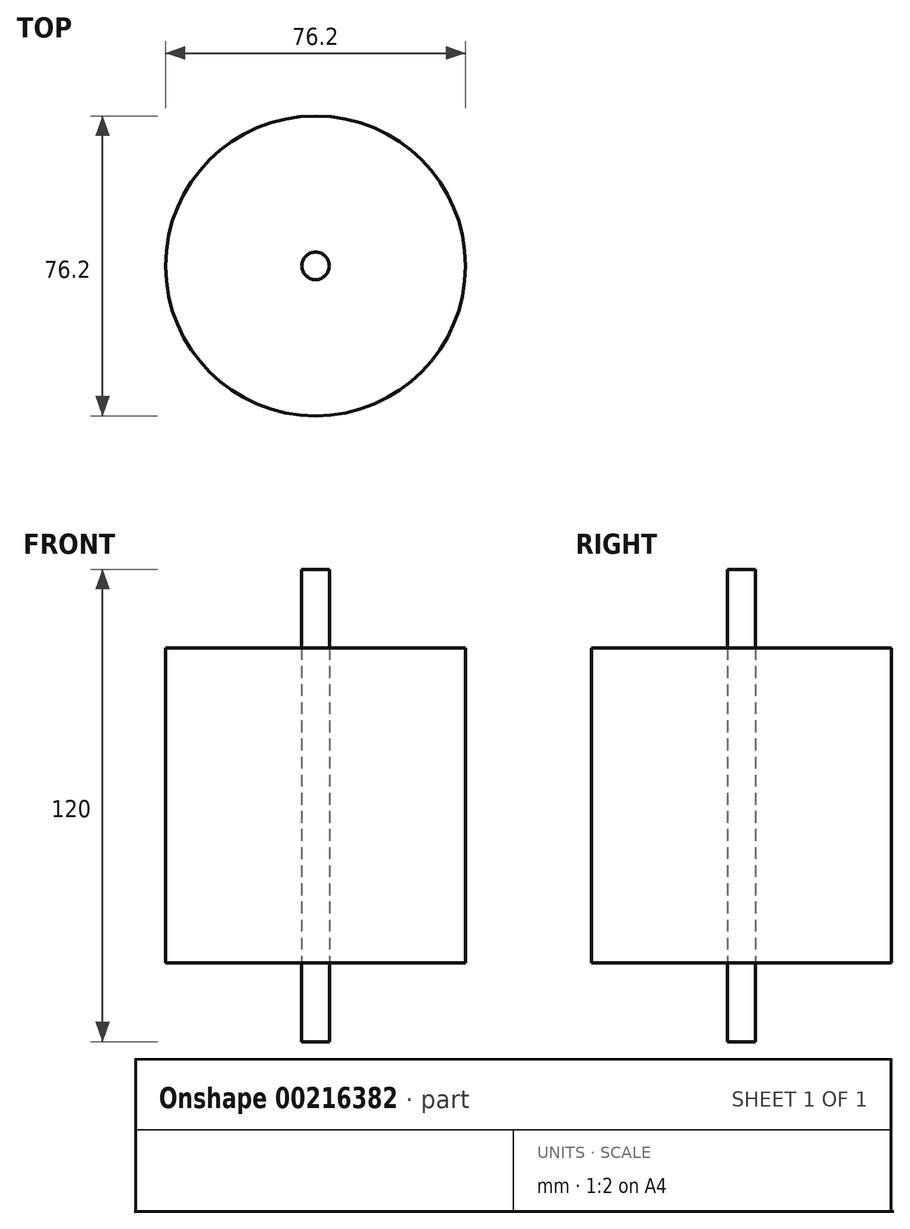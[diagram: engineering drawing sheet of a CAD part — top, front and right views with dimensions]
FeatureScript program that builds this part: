
annotation { "Feature Type Name" : "Feature", "Feature Type Description" : "" }
export const myFeature = defineFeature(function(context is Context, id is Id, definition is map)
    precondition{}
    {
        {
            var Q0;
            Q0=qCreatedBy(makeId("Top.planeOp"),FACE);
            var sketch = newSketch(context, id + "F0", { "sketchPlane" : qUnion([Q0])});
            skCircle(sketch, "E0", {"center": v(0, 0) * mm, "radius": 38.1 * mm});
            skSolve(sketch);
        }
        {
            var Q0;
            Q0=makeQuery(id+"F0.imprint","IMPRINT",FACE,{"disambiguationData":[TD([[makeQuery(id+"F0.imprint","IMPRINT",EDGE,{"derivedFrom":sQuery(id+"F0.wireOp",EDGE,"E0")}),1.0]])]});
            extrude(context, id + "F1", {"entities" : qUnion([Q0]), "depth" : 80 * mm, "offsetDistance" : 25 * mm});
        }
        {
            var Q0;
            Q0=qCreatedBy(makeId("Top.planeOp"),FACE);
            var sketch = newSketch(context, id + "F2", { "sketchPlane" : qUnion([Q0])});
            skCircle(sketch, "E1", {"center": v(0, 0) * mm, "radius": 3.5 * mm});
            skSolve(sketch);
        }
        {
            var Q0;
            Q0 = qSketchRegion(id + "F2", true);
            extrude(context, id + "F3", {"entities" : qUnion([Q0]), "depth" : 100 * mm, "offsetDistance" : 25 * mm, "hasSecondDirection" : true, "secondDirectionOppositeDirection" : true, "secondDirectionDepth" : 20 * mm});
        }
    });
